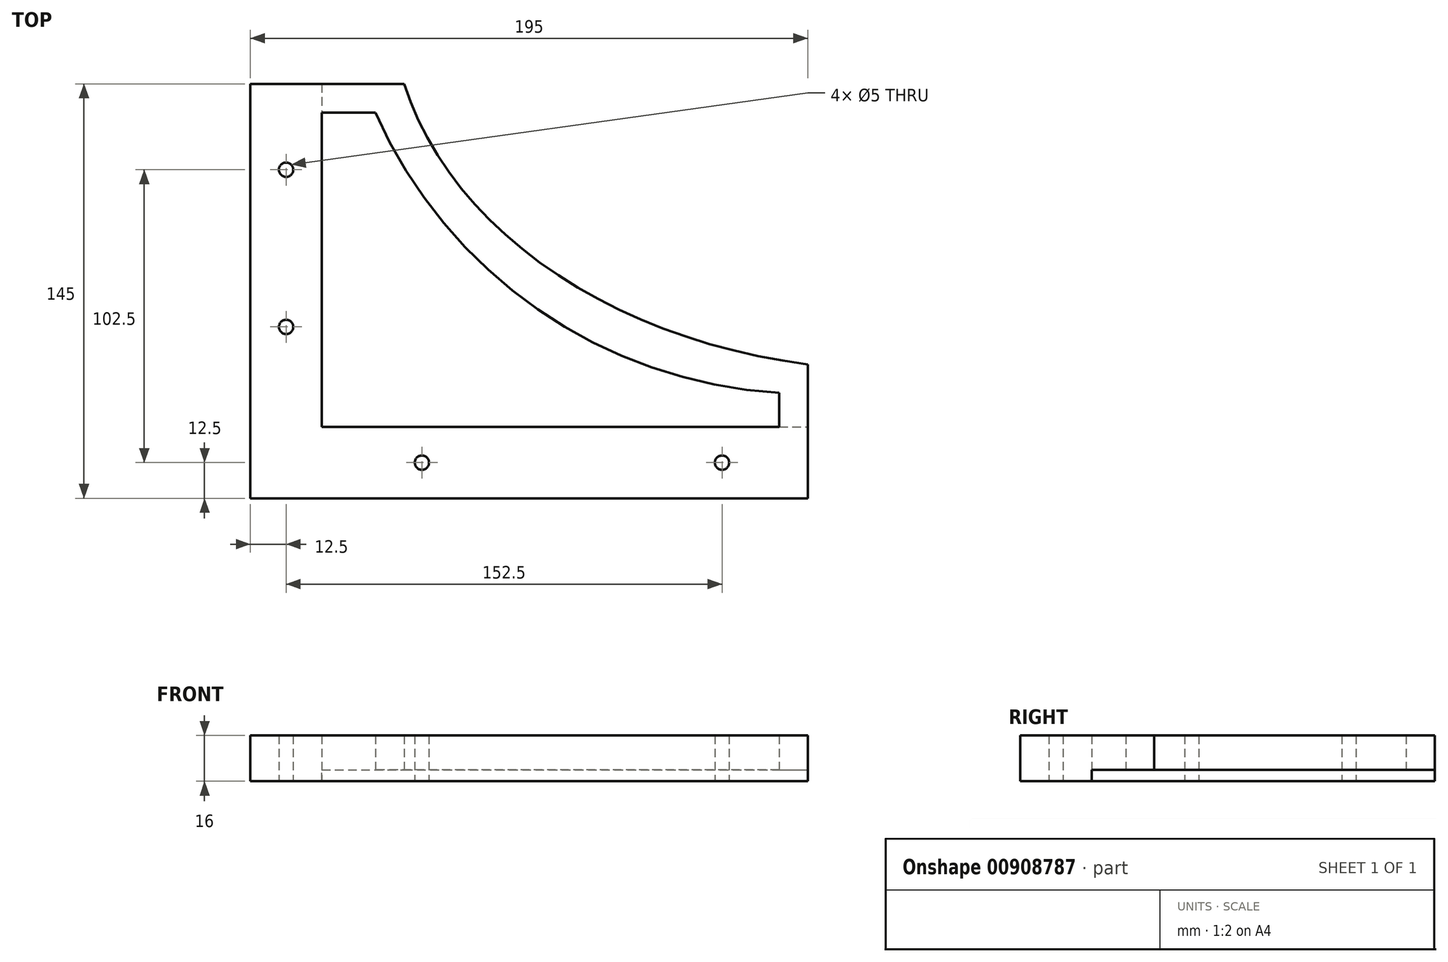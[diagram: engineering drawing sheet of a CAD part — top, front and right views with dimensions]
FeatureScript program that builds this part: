
annotation { "Feature Type Name" : "Feature", "Feature Type Description" : "" }
export const myFeature = defineFeature(function(context is Context, id is Id, definition is map)
    precondition{}
    {
        {
            var Q0;
            Q0=qCreatedBy(makeId("Top.planeOp"),FACE);
            var sketch = newSketch(context, id + "F0", { "sketchPlane" : qUnion([Q0])});
            skEllipticalArc(sketch, "E0", {});
            skLineSegment(sketch, "E1", {"start": v(-176, 0) * mm, "end": v(-176, -130) * mm});
            skPoint(sketch, "E1.endSnap0", {"position": v(0, -130) * mm});
            skLineSegment(sketch, "E2", {"start": v(-176, -130) * mm, "end": v(0, -130) * mm});
            skLineSegment(sketch, "E3", {"start": v(-176, 0) * mm, "end": v(-200, 0) * mm});
            skLineSegment(sketch, "E4", {"start": v(-200, 0) * mm, "end": v(-200, -150) * mm});
            skLineSegment(sketch, "E5", {"start": v(-200, -150) * mm, "end": v(0, -150) * mm});
            skLineSegment(sketch, "E6", {"start": v(0, -150) * mm, "end": v(0, -130) * mm});
            const initialGuessF0  = {"E0": [0, 0, 1, 0, 0.176, 0.13, 3.141592653589793, 4.71238898038469]};
            skSetInitialGuess(sketch, initialGuessF0);
            skSolve(sketch);
        }
        {
            var Q0;
            Q0=qSketchRegion(id+"F0",true);
            extrude(context, id + "F1", {"entities" : qUnion([Q0]), "depth" : 12 * mm, "offsetDistance" : 25 * mm});
        }
        {
            var Q0;
            Q0=makeQuery(id+"F1.opExtrude","SWEPT_FACE",FACE,{"disambiguationData":[OSD([sQuery(id+"F0.wireOp",EDGE,"E5")])]});
            var sketch = newSketch(context, id + "F2", { "sketchPlane" : qUnion([Q0])});
            skLineSegment(sketch, "E7.bottom", {"start": v(-200, 16) * mm, "end": v(0, 16) * mm});
            skLineSegment(sketch, "E7.top", {"start": v(-200, -4) * mm, "end": v(0, -4) * mm});
            skLineSegment(sketch, "E7.left", {"start": v(-200, 16) * mm, "end": v(-200, -4) * mm});
            skLineSegment(sketch, "E7.right", {"start": v(0, 16) * mm, "end": v(0, -4) * mm});
            skSolve(sketch);
        }
        {
            var Q0;
            Q0=qSketchRegion(id+"F2",true);
            extrude(context, id + "F3", {"entities" : qUnion([Q0]), "operationType" : NewBodyOperationType.ADD, "depth" : 5 * mm, "offsetDistance" : 25 * mm});
        }
        {
            var Q0;
            Q0=makeQuery(id+"F3.boolean.opBoolean","MERGE",FACE,{"derivedFrom":[makeQuery(id+"F1.opExtrude","SWEPT_FACE",FACE,{"disambiguationData":[OSD([sQuery(id+"F0.wireOp",EDGE,"E4")])]}),makeQuery(id+"F3.opExtrude","SWEPT_FACE",FACE,{"disambiguationData":[OSD([sQuery(id+"F2.wireOp",EDGE,"E7.left")])]})]});
            var sketch = newSketch(context, id + "F4", { "sketchPlane" : qUnion([Q0])});
            skLineSegment(sketch, "E8.bottom", {"start": v(155, 16) * mm, "end": v(0, 16) * mm});
            skLineSegment(sketch, "E8.top", {"start": v(155, -4) * mm, "end": v(0, -4) * mm});
            skLineSegment(sketch, "E8.left", {"start": v(155, 16) * mm, "end": v(155, -4) * mm});
            skLineSegment(sketch, "E8.right", {"start": v(0, 16) * mm, "end": v(0, -4) * mm});
            skSolve(sketch);
        }
        {
            var Q0;
            Q0=qSketchRegion(id+"F4",true);
            extrude(context, id + "F5", {"entities" : qUnion([Q0]), "operationType" : NewBodyOperationType.ADD, "depth" : 5 * mm, "offsetDistance" : 25 * mm});
        }
        {
            var Q0;
            Q0=makeQuery(id+"F5.boolean.opBoolean","MERGE",FACE,{"derivedFrom":[makeQuery(id+"F3.opExtrude","SWEPT_FACE",FACE,{"disambiguationData":[OSD([sQuery(id+"F2.wireOp",EDGE,"E7.top")])]}),makeQuery(id+"F5.opExtrude","SWEPT_FACE",FACE,{"disambiguationData":[OSD([sQuery(id+"F4.wireOp",EDGE,"E8.top")])]})]});
            var sketch = newSketch(context, id + "F6", { "sketchPlane" : qUnion([Q0])});
            skLineSegment(sketch, "E9", {"start": v(0, 175) * mm, "end": v(-225, 175) * mm});
            skLineSegment(sketch, "E10", {"start": v(-225, 175) * mm, "end": v(-225, 0) * mm});
            skLineSegment(sketch, "E11", {"start": v(-225, 0) * mm, "end": v(-205, 0) * mm});
            skLineSegment(sketch, "E12", {"start": v(-205, 0) * mm, "end": v(-205, 155) * mm});
            skLineSegment(sketch, "E13", {"start": v(-205, 155) * mm, "end": v(0, 155) * mm});
            skLineSegment(sketch, "E14", {"start": v(0, 155) * mm, "end": v(0, 175) * mm});
            skCircle(sketch, "E15", {"center": v(-212.5, 60) * mm, "radius": 2.5 * mm});
            skCircle(sketch, "E16", {"center": v(-212.5, 115) * mm, "radius": 2.5 * mm});
            skCircle(sketch, "E17", {"center": v(-165, 162.5) * mm, "radius": 2.5 * mm});
            skCircle(sketch, "E18", {"center": v(-60, 162.5) * mm, "radius": 2.5 * mm});
            skSolve(sketch);
        }
        {
            var Q0;
            Q0=qSketchRegion(id+"F6",true);
            extrude(context, id + "F7", {"entities" : qUnion([Q0]), "operationType" : NewBodyOperationType.ADD, "oppositeDirection" : true, "depth" : 25 * mm, "offsetDistance" : 25 * mm});
        }
        {
            var Q0;
            Q0=makeQuery(id+"F5.boolean.opBoolean","MERGE",FACE,{"derivedFrom":[makeQuery(id+"F3.opExtrude","SWEPT_FACE",FACE,{"disambiguationData":[OSD([sQuery(id+"F2.wireOp",EDGE,"E7.bottom")])]}),makeQuery(id+"F5.opExtrude","SWEPT_FACE",FACE,{"disambiguationData":[OSD([sQuery(id+"F4.wireOp",EDGE,"E8.bottom")])]})]});
            var sketch = newSketch(context, id + "F8", { "sketchPlane" : qUnion([Q0])});
            skLineSegment(sketch, "E19", {"start": v(-205, 0) * mm, "end": v(-190, 0) * mm});
            skLineSegment(sketch, "E20", {"start": v(-190, 0) * mm, "end": v(-190, -140) * mm});
            skLineSegment(sketch, "E21", {"start": v(-190, -140) * mm, "end": v(0, -140) * mm});
            skLineSegment(sketch, "E22", {"start": v(0, -140) * mm, "end": v(0, -155) * mm});
            skLineSegment(sketch, "E23", {"start": v(0, -155) * mm, "end": v(-205, -155) * mm});
            skLineSegment(sketch, "E24", {"start": v(-205, -155) * mm, "end": v(-205, 0) * mm});
            skSolve(sketch);
        }
        {
            var Q0;
            Q0=qSketchRegion(id+"F8",true);
            extrude(context, id + "F9", {"entities" : qUnion([Q0]), "operationType" : NewBodyOperationType.ADD, "depth" : 5 * mm, "offsetDistance" : 25 * mm});
        }
        {
            var Q0;
            Q0=qCreatedBy(makeId("Top.planeOp"),FACE);
            var sketch = newSketch(context, id + "F10", { "sketchPlane" : qUnion([Q0])});
            skLineSegment(sketch, "E25.bottom", {"start": v(-225, 0) * mm, "end": v(0, 0) * mm});
            skLineSegment(sketch, "E25.top", {"start": v(-225, -30) * mm, "end": v(0, -30) * mm});
            skLineSegment(sketch, "E25.left", {"start": v(-225, 0) * mm, "end": v(-225, -30) * mm});
            skLineSegment(sketch, "E25.right", {"start": v(0, 0) * mm, "end": v(0, -30) * mm});
            skLineSegment(sketch, "E26.bottom", {"start": v(0, -175) * mm, "end": v(-30, -175) * mm});
            skLineSegment(sketch, "E26.top", {"start": v(0, 0) * mm, "end": v(-30, 0) * mm});
            skLineSegment(sketch, "E26.left", {"start": v(0, -175) * mm, "end": v(0, 0) * mm});
            skLineSegment(sketch, "E26.right", {"start": v(-30, -175) * mm, "end": v(-30, 0) * mm});
            skSolve(sketch);
        }
        {
            var Q0;
            Q0=qSketchRegion(id+"F10",true);
            extrude(context, id + "F11", {"entities" : qUnion([Q0]), "operationType" : NewBodyOperationType.REMOVE, "endBound" : BoundingType.SYMMETRIC, "oppositeDirection" : true, "depth" : 50 * mm, "offsetDistance" : 25 * mm});
        }
        {
            var Q0;
            Q0=makeQuery(id+"F11.boolean.opBoolean","COPY",FACE,{"derivedFrom":makeQuery(id+"F11.opExtrude","SWEPT_FACE",FACE,{"disambiguationData":[OSD([sQuery(id+"F10.wireOp",EDGE,"E26.right")])]})});
            var sketch = newSketch(context, id + "F12", { "sketchPlane" : qUnion([Q0])});
            skLineSegment(sketch, "E27.bottom", {"start": v(-175, 21) * mm, "end": v(-30, 21) * mm});
            skLineSegment(sketch, "E27.top", {"start": v(-175, 12) * mm, "end": v(-30, 12) * mm});
            skLineSegment(sketch, "E27.left", {"start": v(-175, 21) * mm, "end": v(-175, 12) * mm});
            skLineSegment(sketch, "E27.right", {"start": v(-30, 21) * mm, "end": v(-30, 12) * mm});
            skSolve(sketch);
        }
        {
            var Q0;
            Q0=qSketchRegion(id+"F12",true);
            extrude(context, id + "F13", {"entities" : qUnion([Q0]), "operationType" : NewBodyOperationType.REMOVE, "endBound" : BoundingType.THROUGH_ALL, "oppositeDirection" : true, "depth" : 25 * mm, "offsetDistance" : 25 * mm});
        }
        {
            var Q0;
            Q0=makeQuery(id+"F1.opExtrude","CAP_FACE",FACE,{"disambiguationData":[OSD([sQuery(id+"F0.wireOp",EDGE,"E0"),sQuery(id+"F0.wireOp",EDGE,"E3"),sQuery(id+"F0.wireOp",EDGE,"E4"),sQuery(id+"F0.wireOp",EDGE,"E5"),sQuery(id+"F0.wireOp",EDGE,"E6")])],"isStart":true});
            var sketch = newSketch(context, id + "F14", { "sketchPlane" : qUnion([Q0])});
            skLineSegment(sketch, "E28", {"start": v(-40, 138.1) * mm, "end": v(-40, 150) * mm});
            skLineSegment(sketch, "E29", {"start": v(-40, 150) * mm, "end": v(-200, 150) * mm});
            skLineSegment(sketch, "E30", {"start": v(-200, 150) * mm, "end": v(-200, 40) * mm});
            skLineSegment(sketch, "E31", {"start": v(-200, 40) * mm, "end": v(-181.25, 40) * mm});
            skArc(sketch, "E32", {"start": v(-40, 138.1) * mm, "mid": v(-124.42, 108.9) * mm, "end": v(-181.25, 40) * mm});
            skSolve(sketch);
        }
        {
            var Q0;
            Q0 = qSketchRegion(id + "F14", true);
            extrude(context, id + "F15", {"entities" : qUnion([Q0]), "operationType" : NewBodyOperationType.REMOVE, "oppositeDirection" : true, "depth" : 25 * mm, "offsetDistance" : 25 * mm});
        }
    });
